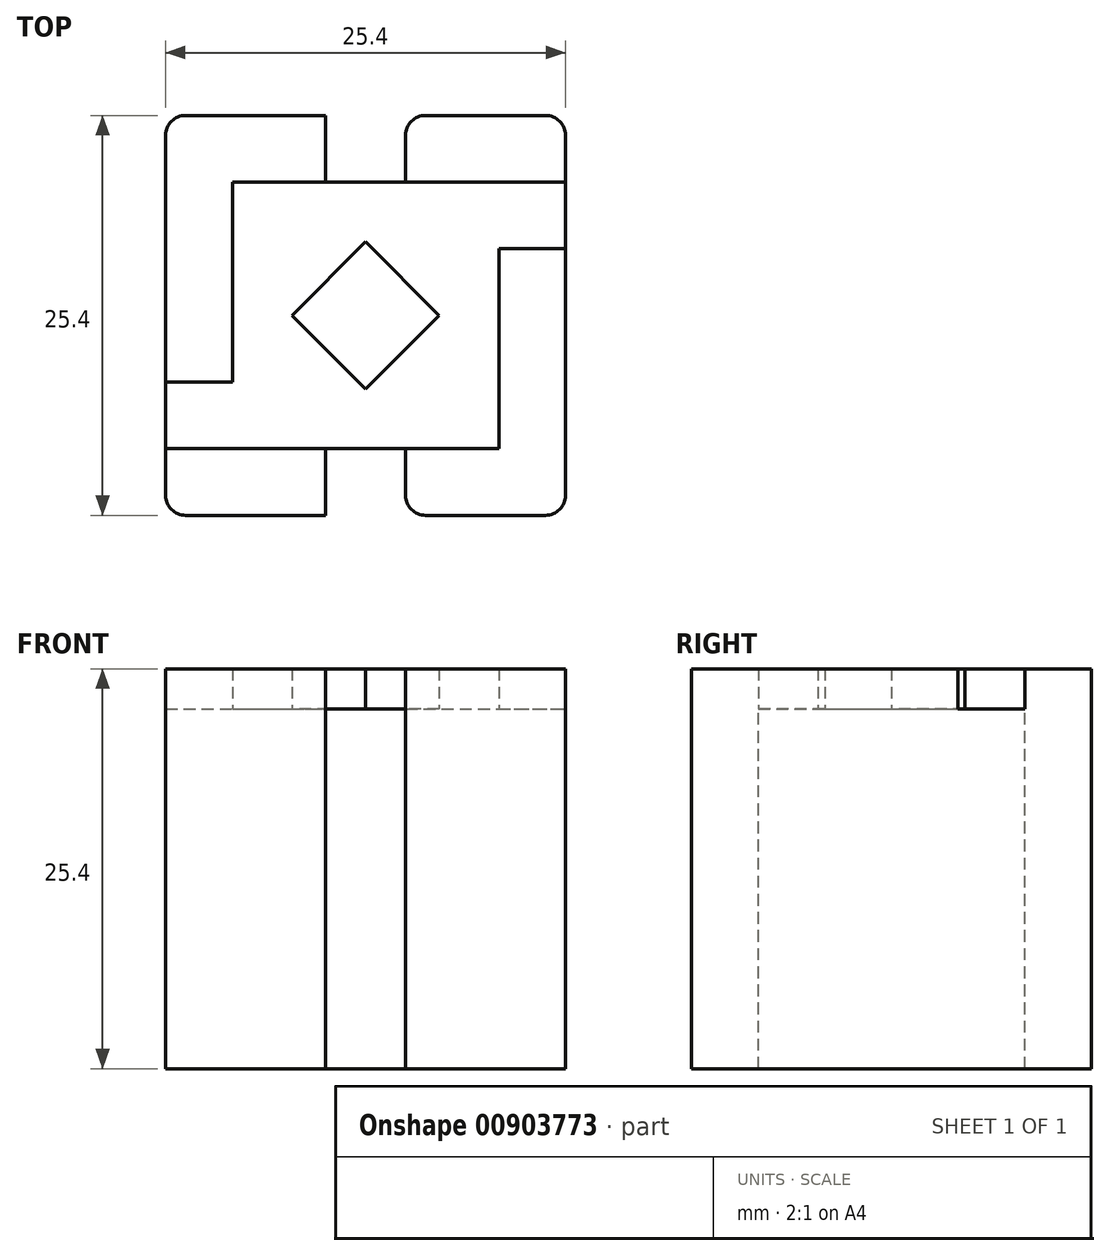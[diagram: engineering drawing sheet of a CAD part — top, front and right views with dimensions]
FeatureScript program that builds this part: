
annotation { "Feature Type Name" : "Feature", "Feature Type Description" : "" }
export const myFeature = defineFeature(function(context is Context, id is Id, definition is map)
    precondition{}
    {
        {
            var Q0;
            Q0=qCreatedBy(makeId("Top.planeOp"),FACE);
            var sketch = newSketch(context, id + "F0", { "sketchPlane" : qUnion([Q0])});
            skLineSegment(sketch, "E0.bottom", {"start": v(-12.7, 12.7) * mm, "end": v(12.7, 12.7) * mm});
            skLineSegment(sketch, "E0.top", {"start": v(-12.7, -12.7) * mm, "end": v(12.7, -12.7) * mm});
            skLineSegment(sketch, "E0.left", {"start": v(-12.7, 12.7) * mm, "end": v(-12.7, -12.7) * mm});
            skLineSegment(sketch, "E0.right", {"start": v(12.7, 12.7) * mm, "end": v(12.7, -12.7) * mm});
            skPoint(sketch, "E0.middle", {"position": v(0, 0) * mm});
            skSolve(sketch);
        }
        {
            var Q0;
            Q0 = qSketchRegion(id + "F0", true);
            extrude(context, id + "F1", {"entities" : qUnion([Q0]), "endBound" : BoundingType.SYMMETRIC, "depth" : 22.86 * mm, "offsetDistance" : 25.4 * mm});
        }
        {
            var Q0;
            Q0=makeQuery(id+"F1.opExtrude","CAP_FACE",FACE,{"disambiguationData":[OSD([sQuery(id+"F0.wireOp",EDGE,"E0.bottom"),sQuery(id+"F0.wireOp",EDGE,"E0.top"),sQuery(id+"F0.wireOp",EDGE,"E0.left"),sQuery(id+"F0.wireOp",EDGE,"E0.right")])],"isStart":false});
            var sketch = newSketch(context, id + "F2", { "sketchPlane" : qUnion([Q0])});
            skLineSegment(sketch, "E1", {"start": v(-12.7, 12.7) * mm, "end": v(-12.7, -4.23) * mm});
            skLineSegment(sketch, "E2", {"start": v(-12.7, -4.23) * mm, "end": v(-8.46, -4.23) * mm});
            skLineSegment(sketch, "E3", {"start": v(-8.46, -4.23) * mm, "end": v(-8.46, 8.47) * mm});
            skLineSegment(sketch, "E4", {"start": v(-8.46, 8.47) * mm, "end": v(-2.54, 8.47) * mm});
            skLineSegment(sketch, "E5", {"start": v(-2.54, 8.47) * mm, "end": v(-2.54, 12.7) * mm});
            skLineSegment(sketch, "E6", {"start": v(-2.54, 12.7) * mm, "end": v(-12.7, 12.7) * mm});
            skLineSegment(sketch, "E7", {"start": v(12.7, 12.7) * mm, "end": v(2.54, 12.7) * mm});
            skLineSegment(sketch, "E8", {"start": v(2.54, 12.7) * mm, "end": v(2.54, 8.47) * mm});
            skLineSegment(sketch, "E9", {"start": v(2.54, 8.47) * mm, "end": v(12.7, 8.47) * mm});
            skLineSegment(sketch, "E10", {"start": v(12.7, 8.47) * mm, "end": v(12.7, 12.7) * mm});
            skLineSegment(sketch, "E11.bottom", {"start": v(-12.7, -12.7) * mm, "end": v(-2.54, -12.7) * mm});
            skLineSegment(sketch, "E11.top", {"start": v(-12.7, -8.46) * mm, "end": v(-2.54, -8.46) * mm});
            skLineSegment(sketch, "E11.left", {"start": v(-12.7, -12.7) * mm, "end": v(-12.7, -8.46) * mm});
            skLineSegment(sketch, "E11.right", {"start": v(-2.54, -12.7) * mm, "end": v(-2.54, -8.46) * mm});
            skLineSegment(sketch, "E12", {"start": v(12.7, -12.7) * mm, "end": v(2.54, -12.7) * mm});
            skLineSegment(sketch, "E13", {"start": v(2.54, -12.7) * mm, "end": v(2.54, -8.46) * mm});
            skLineSegment(sketch, "E14", {"start": v(2.54, -8.46) * mm, "end": v(8.47, -8.46) * mm});
            skLineSegment(sketch, "E15", {"start": v(8.47, -8.46) * mm, "end": v(8.47, 4.23) * mm});
            skLineSegment(sketch, "E16", {"start": v(8.47, 4.23) * mm, "end": v(12.7, 4.23) * mm});
            skLineSegment(sketch, "E17", {"start": v(12.7, 4.23) * mm, "end": v(12.7, -12.7) * mm});
            skLineSegment(sketch, "E18", {"start": v(0, 4.67) * mm, "end": v(-4.67, 0) * mm});
            skLineSegment(sketch, "E19", {"start": v(-4.67, 0) * mm, "end": v(0, -4.67) * mm});
            skLineSegment(sketch, "E20", {"start": v(0, -4.67) * mm, "end": v(4.67, 0) * mm});
            skLineSegment(sketch, "E21", {"start": v(4.67, 0) * mm, "end": v(0, 4.67) * mm});
            skLineSegment(sketch, "E22", {"start": v(-2.54, 8.47) * mm, "end": v(2.54, 8.47) * mm});
            skLineSegment(sketch, "E23", {"start": v(2.54, -8.46) * mm, "end": v(-2.54, -8.46) * mm});
            skSolve(sketch);
        }
        {
            var Q0;
            Q0=makeQuery(id+"F2.imprint","IMPRINT",FACE,{"disambiguationData":[TD([[makeQuery(id+"F2.imprint","IMPRINT",EDGE,{"derivedFrom":sQuery(id+"F2.wireOp",EDGE,"E1")}),1.0]])]});
            var Q1;
            Q1=makeQuery(id+"F2.imprint","IMPRINT",FACE,{"disambiguationData":[TD([[makeQuery(id+"F2.imprint","IMPRINT",EDGE,{"derivedFrom":sQuery(id+"F2.wireOp",EDGE,"E7")}),-1.0]])]});
            var Q2;
            Q2=makeQuery(id+"F2.imprint","IMPRINT",FACE,{"disambiguationData":[TD([[makeQuery(id+"F2.imprint","IMPRINT",EDGE,{"derivedFrom":sQuery(id+"F2.wireOp",EDGE,"E12")}),1.0]])]});
            var Q3;
            Q3=makeQuery(id+"F2.imprint","IMPRINT",FACE,{"disambiguationData":[TD([[makeQuery(id+"F2.imprint","IMPRINT",EDGE,{"derivedFrom":sQuery(id+"F2.wireOp",EDGE,"E18")}),1.0]])]});
            var Q4;
            Q4=makeQuery(id+"F2.imprint","IMPRINT",FACE,{"disambiguationData":[TD([[makeQuery(id+"F2.imprint","IMPRINT",EDGE,{"derivedFrom":sQuery(id+"F2.wireOp",EDGE,"E11.bottom")}),1.0]])]});
            extrude(context, id + "F3", {"entities" : qUnion([Q0, Q1, Q2, Q3, Q4]), "operationType" : NewBodyOperationType.ADD, "depth" : 2.54 * mm, "offsetDistance" : 25.4 * mm});
        }
        {
            var Q0;
            {var subQ0=sQuery(id+"F2.wireOp",EDGE,"E5");Q0=makeQuery(id+"F2.imprint","IMPRINT",FACE,{"disambiguationData":[TD([[makeQuery(id+"F2.imprint","IMPRINT",EDGE,{"derivedFrom":subQ0}),-1.0]])]});}
            var Q1;
            {var subQ0=sQuery(id+"F2.wireOp",EDGE,"E11.right");Q1=makeQuery(id+"F2.imprint","IMPRINT",FACE,{"disambiguationData":[TD([[makeQuery(id+"F2.imprint","IMPRINT",EDGE,{"derivedFrom":subQ0}),-1.0]])]});}
            extrude(context, id + "F4", {"entities" : qUnion([Q0, Q1]), "operationType" : NewBodyOperationType.REMOVE, "endBound" : BoundingType.THROUGH_ALL, "oppositeDirection" : true, "depth" : 25.4 * mm, "offsetDistance" : 25.4 * mm});
        }
        {
            var Q0;
            Q0=makeQuery(id+"F3.boolean.opBoolean","MERGE",EDGE,{"derivedFrom":[makeQuery(id+"F1.opExtrude","SWEPT_EDGE",EDGE,{"disambiguationData":[OSD([sQuery(id+"F0.wireOp",EDGE,"E0.bottom"),sQuery(id+"F0.wireOp",EDGE,"E0.left")])]}),makeQuery(id+"F3.opExtrude","SWEPT_EDGE",EDGE,{"disambiguationData":[OSD([sQuery(id+"F2.wireOp",EDGE,"E1"),sQuery(id+"F2.wireOp",EDGE,"E6")])]})]});
            var Q1;
            Q1=makeQuery(id+"F3.boolean.opBoolean","MERGE",EDGE,{"derivedFrom":[makeQuery(id+"F1.opExtrude","SWEPT_EDGE",EDGE,{"disambiguationData":[OSD([sQuery(id+"F0.wireOp",EDGE,"E0.top"),sQuery(id+"F0.wireOp",EDGE,"E0.left")])]}),makeQuery(id+"F3.opExtrude","SWEPT_EDGE",EDGE,{"disambiguationData":[OSD([sQuery(id+"F2.wireOp",EDGE,"E11.bottom"),sQuery(id+"F2.wireOp",EDGE,"E11.left")])]})]});
            var Q2;
            Q2=makeQuery(id+"F3.boolean.opBoolean","MERGE",EDGE,{"derivedFrom":[makeQuery(id+"F1.opExtrude","SWEPT_EDGE",EDGE,{"disambiguationData":[OSD([sQuery(id+"F0.wireOp",EDGE,"E0.bottom"),sQuery(id+"F0.wireOp",EDGE,"E0.right")])]}),makeQuery(id+"F3.opExtrude","SWEPT_EDGE",EDGE,{"disambiguationData":[OSD([sQuery(id+"F2.wireOp",EDGE,"E7"),sQuery(id+"F2.wireOp",EDGE,"E10")])]})]});
            var Q3;
            Q3=makeQuery(id+"F3.boolean.opBoolean","MERGE",EDGE,{"derivedFrom":[makeQuery(id+"F1.opExtrude","SWEPT_EDGE",EDGE,{"disambiguationData":[OSD([sQuery(id+"F0.wireOp",EDGE,"E0.top"),sQuery(id+"F0.wireOp",EDGE,"E0.right")])]}),makeQuery(id+"F3.opExtrude","SWEPT_EDGE",EDGE,{"disambiguationData":[OSD([sQuery(id+"F2.wireOp",EDGE,"E12"),sQuery(id+"F2.wireOp",EDGE,"E17")])]})]});
            var Q4;
            {var subQ0=sQuery(id+"F2.wireOp",EDGE,"E13");var subQ1=sQuery(id+"F2.wireOp",EDGE,"E12");var subQ2=sQuery(id+"F0.wireOp",EDGE,"E0.top");Q4=makeQuery(id+"F4.boolean.opBoolean","MERGE",EDGE,{"derivedFrom":[makeQuery(id+"F3.opExtrude","SWEPT_EDGE",EDGE,{"disambiguationData":[OSD([subQ2,subQ1,subQ0])]})],"fromTools":[makeQuery(id+"F4.opExtrude","SWEPT_EDGE",EDGE,{"disambiguationData":[OSD([subQ2,subQ1,subQ0])]})]});}
            var Q5;
            {var subQ0=sQuery(id+"F2.wireOp",EDGE,"E11.right");var subQ1=sQuery(id+"F2.wireOp",EDGE,"E11.bottom");var subQ2=sQuery(id+"F0.wireOp",EDGE,"E0.top");Q5=makeQuery(id+"F4.boolean.opBoolean","MERGE",EDGE,{"derivedFrom":[makeQuery(id+"F3.opExtrude","SWEPT_EDGE",EDGE,{"disambiguationData":[OSD([subQ2,subQ1,subQ0])]})],"fromTools":[makeQuery(id+"F4.opExtrude","SWEPT_EDGE",EDGE,{"disambiguationData":[OSD([subQ2,subQ1,subQ0])]})]});}
            var Q6;
            {var subQ0=sQuery(id+"F2.wireOp",EDGE,"E8");var subQ1=sQuery(id+"F2.wireOp",EDGE,"E7");var subQ2=sQuery(id+"F0.wireOp",EDGE,"E0.bottom");Q6=makeQuery(id+"F4.boolean.opBoolean","MERGE",EDGE,{"derivedFrom":[makeQuery(id+"F3.opExtrude","SWEPT_EDGE",EDGE,{"disambiguationData":[OSD([subQ2,subQ1,subQ0])]})],"fromTools":[makeQuery(id+"F4.opExtrude","SWEPT_EDGE",EDGE,{"disambiguationData":[OSD([subQ2,subQ1,subQ0])]})]});}
            var Q7;
            {var subQ0=sQuery(id+"F2.wireOp",EDGE,"E6");var subQ1=sQuery(id+"F2.wireOp",EDGE,"E5");var subQ2=sQuery(id+"F0.wireOp",EDGE,"E0.bottom");Q7=makeQuery(id+"F4.boolean.opBoolean","MERGE",EDGE,{"derivedFrom":[makeQuery(id+"F3.opExtrude","SWEPT_EDGE",EDGE,{"disambiguationData":[OSD([subQ2,subQ1,subQ0])]})],"fromTools":[makeQuery(id+"F4.opExtrude","SWEPT_EDGE",EDGE,{"disambiguationData":[OSD([subQ2,subQ1,subQ0])]})]});}
            fillet(context, id + "F5", {"entities" : qUnion([Q0, Q1, Q2, Q3, Q4, Q5, Q6, Q7]), "radius" : 1.27 * mm, "tangentPropagation" : true, "allowEdgeOverflow" : false});
        }
    });
